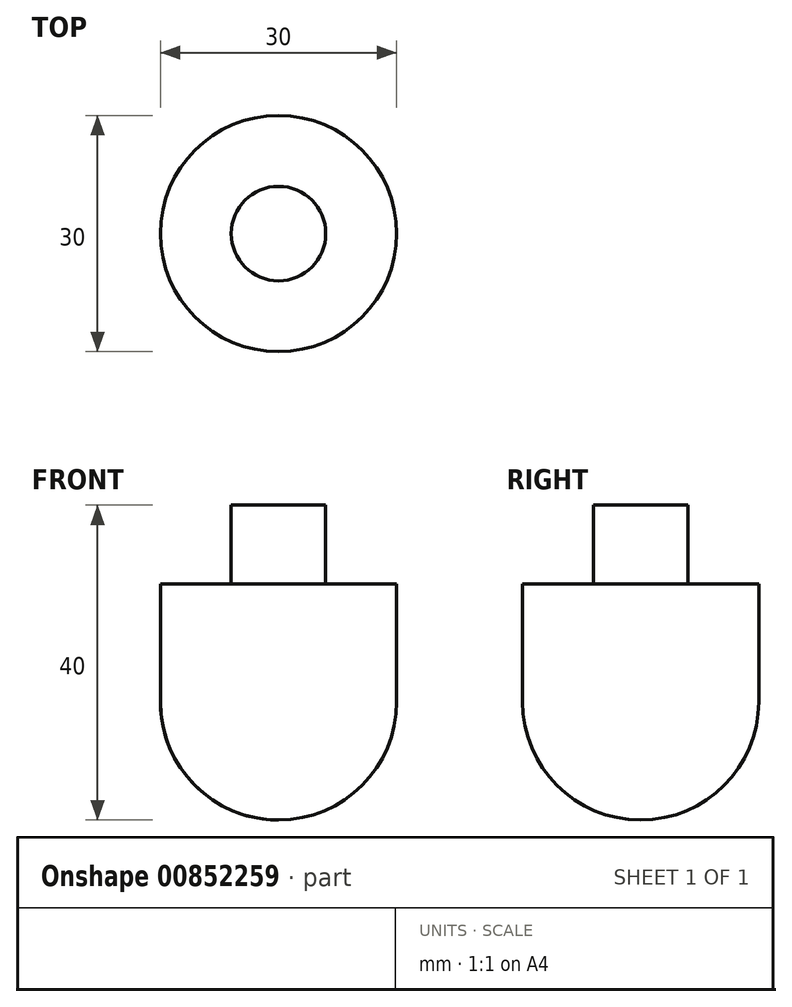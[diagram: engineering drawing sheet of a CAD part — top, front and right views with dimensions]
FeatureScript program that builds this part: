
annotation { "Feature Type Name" : "Feature", "Feature Type Description" : "" }
export const myFeature = defineFeature(function(context is Context, id is Id, definition is map)
    precondition{}
    {
        {
            var Q0;
            Q0=qCreatedBy(makeId("Front.planeOp"),FACE);
            var sketch = newSketch(context, id + "F0", { "sketchPlane" : qUnion([Q0])});
            skLineSegment(sketch, "E0", {"start": v(0, 0) * mm, "end": v(-6, 0) * mm});
            skLineSegment(sketch, "E1", {"start": v(-6, 0) * mm, "end": v(-6, -10) * mm});
            skLineSegment(sketch, "E2", {"start": v(-6, -10) * mm, "end": v(-15, -10) * mm});
            skLineSegment(sketch, "E3", {"start": v(-15, -10) * mm, "end": v(-15, -25) * mm});
            skArc(sketch, "E4", {"start": v(-15, -25) * mm, "mid": v(-10.6, -35.6) * mm, "end": v(0, -40) * mm});
            skLineSegment(sketch, "E5", {"start": v(0, 0) * mm, "end": v(0, -40) * mm});
            skSolve(sketch);
        }
        {
            var Q0;
            Q0 = qSketchRegion(id + "F0", true);
            var Q1;
            Q1=sQuery(id+"F0.wireOp",EDGE,"E5");
            revolve(context, id + "F1", {"surfaceOperationType" : NewSurfaceOperationType.NEW, "entities" : qUnion([Q0]), "axis" : qUnion([Q1]), "revolveType" : RevolveType.FULL});
        }
    });
